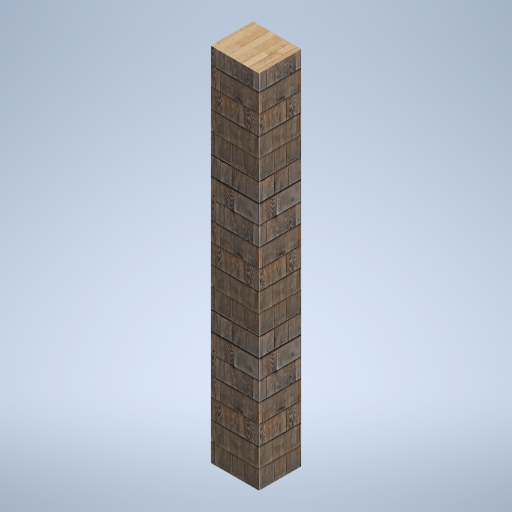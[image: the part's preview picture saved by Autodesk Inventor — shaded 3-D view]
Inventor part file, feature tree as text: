
AUTODESK INVENTOR PART (.ipt)
format: ipt  version: 2024.2 (Build 282272000, 272)  size: 353,792 bytes
history: native  units: in
note: dims shown in document units (in); Inventor stores cm internally (conversion verified against a paired STEP export)
features: other x3, sketch x1
ambient origin geometry x8: Origin, YZ Plane, XZ Plane, XY Plane, X Axis, Y Axis, Z Axis, Center Point
bodies: Solid1 (feature_tree)
feature tree (4):
  other  "support_column_02.ipt"
  other  "Solid1::support_column_02.ipt"
  other  "TaggingFeature1"
  sketch  "Sketch1"  dims[d0=0.3937in]
